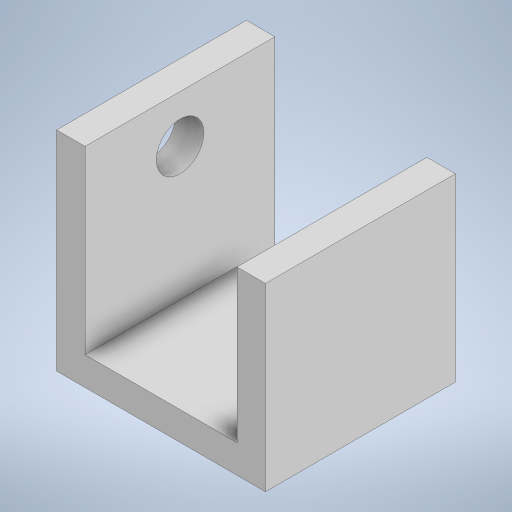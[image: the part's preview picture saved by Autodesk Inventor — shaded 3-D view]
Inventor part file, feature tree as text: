
AUTODESK INVENTOR PART (.ipt)
format: ipt  version: 2023 (Build 270158000, 158)  size: 271,360 bytes
history: native  units: in
note: dims shown in document units (in); Inventor stores cm internally (conversion verified against a paired STEP export)
features: extrude x3, sketch x3
ambient origin geometry x8: Origin, YZ Plane, XZ Plane, XY Plane, X Axis, Y Axis, Z Axis, Center Point
bodies: Solid1 (feature_tree)
feature tree (6):
  extrude  "Extrusion1"  Depth=0.748in
  extrude  "Extrusion2"  Depth=0.1181in
  extrude  "Extrusion3"  Depth=0.7874in TaperAngle=0.0deg
  sketch  "Sketch1"  dims[d0=0.8661in d1=0.748in]
  sketch  "Sketch2"  dims[d2=0.1181in d3=0.1181in]
  sketch  "Sketch3"  dims[d4=0.1181in d5=0.7874in d6=0.0in d7=0.1181in d8=0.1181in d9=0.0in d10=0.3937in d11=0.1969in d12=0.1969in d13=0.1969in d14=0.0in]
